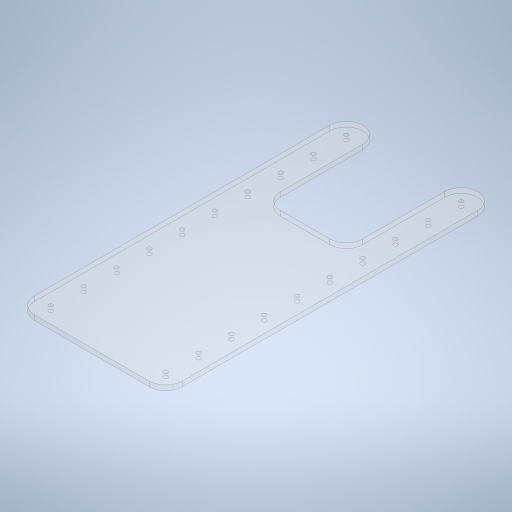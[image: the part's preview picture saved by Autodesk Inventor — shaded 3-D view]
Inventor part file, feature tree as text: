
AUTODESK INVENTOR PART (.ipt)
format: ipt  version: 2023 (Build 270158000, 158)  size: 308,736 bytes
history: native  units: in
note: dims shown in document units (in); Inventor stores cm internally (conversion verified against a paired STEP export)
features: extrude x1
ambient origin geometry x8: Origin, YZ Plane, XZ Plane, XY Plane, X Axis, Y Axis, Z Axis, Center Point
bodies: Body1 (feature_tree)
feature tree (1):
  extrude  "Extrusion2"  Depth=3.5433in
